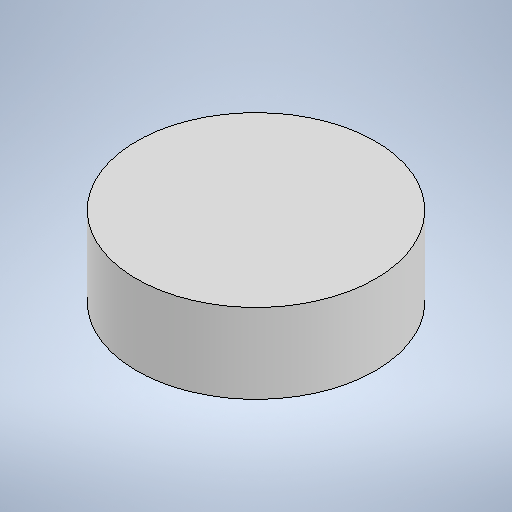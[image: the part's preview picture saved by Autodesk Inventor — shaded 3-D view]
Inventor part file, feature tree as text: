
AUTODESK INVENTOR PART (.ipt)
format: ipt  version: 2025.1 (Build 291241020, 241B)  size: 267,264 bytes
history: native  units: mm
features: sketch x8, extrude x1, revolve x1
ambient origin geometry x8: Origin, YZ Plane, XZ Plane, XY Plane, X Axis, Y Axis, Z Axis, Center Point
bodies: Solid1 (feature_tree)
feature tree (10):
  sketch  "Sketch1"  dims[d0=88.9mm d1=3.0mm]
  sketch  "Sketch2"  dims[d7=120.0mm d9=360.0deg]
  extrude  "Extrusion1"  Depth=3.0mm
  revolve  "Revolution1"  Angle=360.0deg
  sketch  "Sketch Circular Pattern1"  dims[d2=1200.0mm d3=120.0mm d5=360.0deg]
  sketch  "Sketch Circular Pattern2"  dims[d11=200.0mm]
  sketch  "Sketch Circular Pattern3"  dims[d12=120.0mm d14=360.0deg]
  sketch  "Sketch Circular Pattern4"  dims[d20=15.0deg]
  sketch  "Sketch3"  dims[d16=40.0mm d18=360.0deg]
  sketch  "Sketch4"  dims[d21=0.0mm d22=15.0deg d23=45.0deg d24=140.0mm d25=300.0mm d26=460.0mm d27=560.0mm d28=30.0mm d29=10.0mm d30=0.0mm d31=6.0mm d32=1803.421613mm d33=1200.0mm d37=100.0mm d38=30.0mm d39=1200.0mm d40=6.0mm d41=1200.0mm d42=253.289193mm d43=90.0deg]
